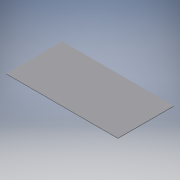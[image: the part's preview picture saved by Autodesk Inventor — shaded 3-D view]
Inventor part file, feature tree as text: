
AUTODESK INVENTOR PART (.ipt)
format: ipt  version: 2016 (Build 200138000, 138)  size: 95,232 bytes
history: native  units: mm
features: extrude x1, sketch x1
ambient origin geometry x8: Origin, YZ Plane, XZ Plane, XY Plane, X Axis, Y Axis, Z Axis, Center Point
bodies: Solid1 (feature_tree)
feature tree (2):
  extrude  "Extrusion1"  [1 undecoded]
  sketch  "Sketch1"  dims[d4=0.0mm]
note: 1 required parameter value undecoded (feature->parameter linkage not recoverable at this tier; creation-order binding heuristic only, values carry confidence <= 0.55)
